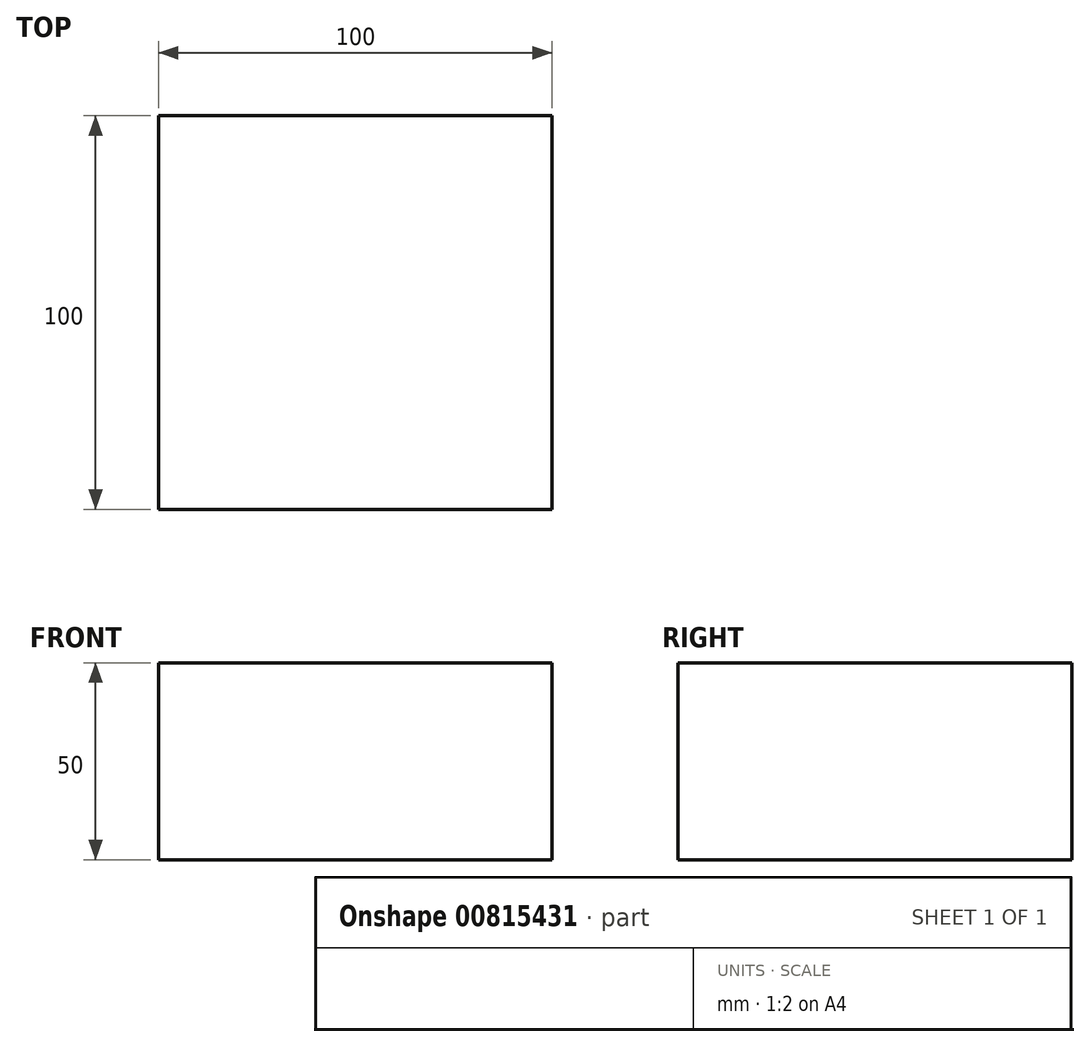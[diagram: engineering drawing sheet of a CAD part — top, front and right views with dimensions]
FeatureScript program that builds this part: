
annotation { "Feature Type Name" : "Feature", "Feature Type Description" : "" }
export const myFeature = defineFeature(function(context is Context, id is Id, definition is map)
    precondition{}
    {
        {
            var Q0;
            Q0=qCreatedBy(makeId("Top.planeOp"),FACE);
            var sketch = newSketch(context, id + "F0", { "sketchPlane" : qUnion([Q0])});
            skCircle(sketch, "E0", {"center": v(0, 0) * mm, "radius": 50 * mm});
            skSolve(sketch);
        }
        {
            var Q0;
            Q0=qCreatedBy(makeId("Right.planeOp"),FACE);
            var sketch = newSketch(context, id + "F1", { "sketchPlane" : qUnion([Q0])});
            skLineSegment(sketch, "E1.bottom", {"start": v(62.74, 54.22) * mm, "end": v(60.7, 54.22) * mm});
            skLineSegment(sketch, "E1.top", {"start": v(62.74, 53.17) * mm, "end": v(60.7, 53.17) * mm});
            skLineSegment(sketch, "E1.left", {"start": v(62.74, 54.22) * mm, "end": v(62.74, 53.17) * mm});
            skLineSegment(sketch, "E1.right", {"start": v(60.7, 54.22) * mm, "end": v(60.7, 53.17) * mm});
            skLineSegment(sketch, "E2.bottom", {"start": v(47.36, 12.4) * mm, "end": v(-52.64, 12.4) * mm});
            skLineSegment(sketch, "E2.top", {"start": v(47.36, -37.6) * mm, "end": v(-52.64, -37.6) * mm});
            skLineSegment(sketch, "E2.left", {"start": v(47.36, 12.4) * mm, "end": v(47.36, -37.6) * mm});
            skLineSegment(sketch, "E2.right", {"start": v(-52.64, 12.4) * mm, "end": v(-52.64, -37.6) * mm});
            skSolve(sketch);
        }
        {
            var Q0;
            Q0=makeQuery(id+"F1.imprint","IMPRINT",FACE,{"disambiguationData":[TD([[makeQuery(id+"F1.imprint","IMPRINT",EDGE,{"derivedFrom":sQuery(id+"F1.wireOp",EDGE,"E2.bottom")}),1.0]])]});
            extrude(context, id + "F2", {"entities" : qUnion([Q0]), "depth" : 100 * mm, "offsetDistance" : 25 * mm});
        }
        {
            var Q0;
            Q0=sQuery(id+"F0.wireOp",EDGE,"E0");
            extrude(context, id + "F3", {"bodyType" : ToolBodyType.SURFACE, "surfaceEntities" : qUnion([Q0]), "depth" : 60 * mm, "offsetDistance" : 25 * mm});
        }
    });
